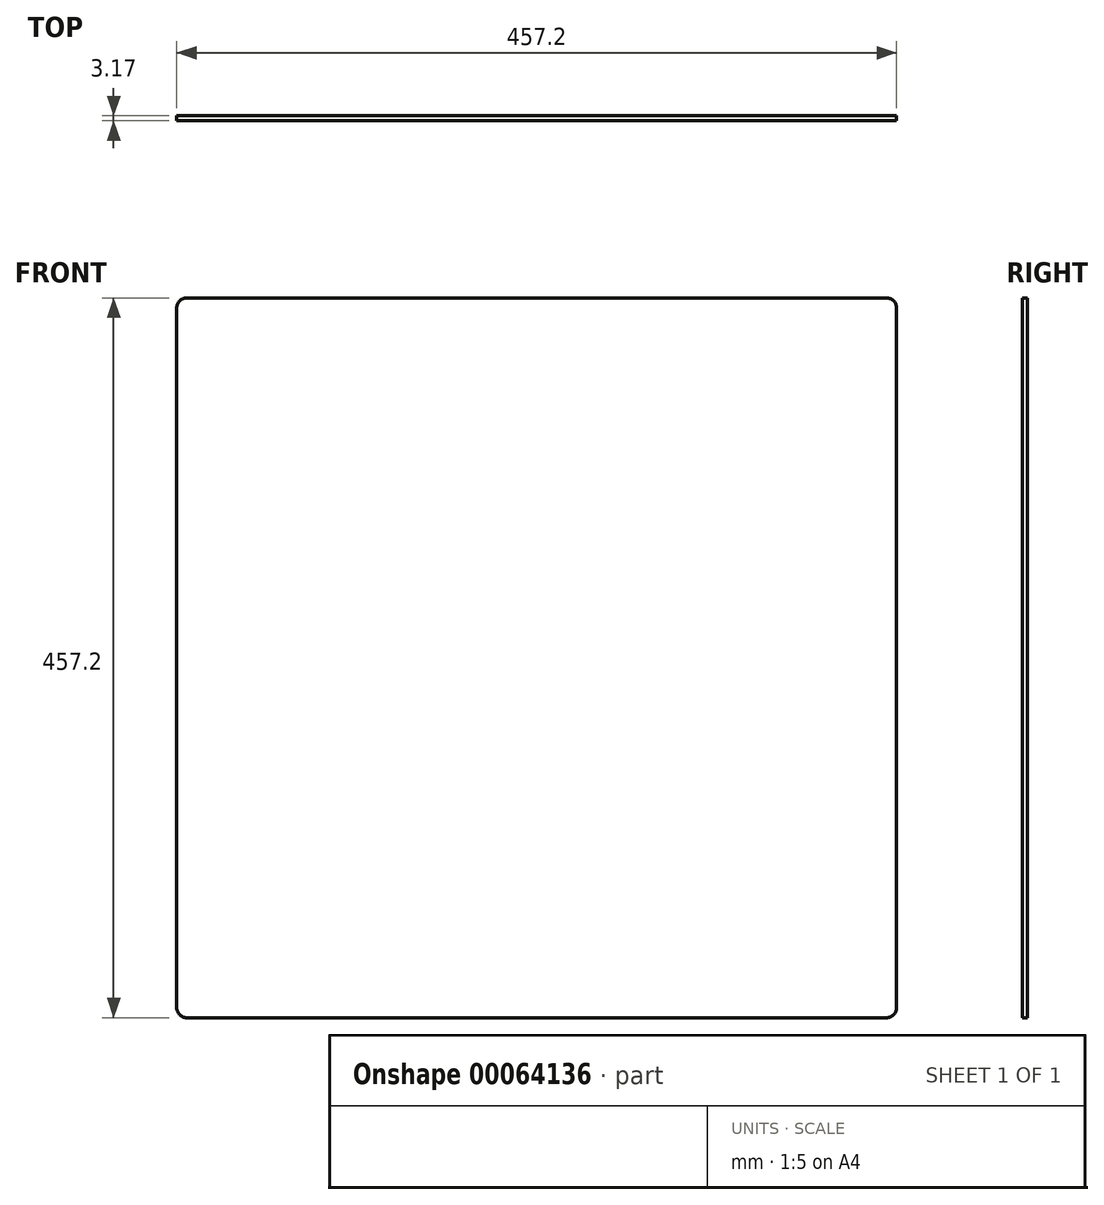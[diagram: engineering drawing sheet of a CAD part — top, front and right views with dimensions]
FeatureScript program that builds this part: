
annotation { "Feature Type Name" : "Feature", "Feature Type Description" : "" }
export const myFeature = defineFeature(function(context is Context, id is Id, definition is map)
    precondition{}
    {
        {
            var Q0;
            Q0=qCreatedBy(makeId("Front.planeOp"),FACE);
            var sketch = newSketch(context, id + "F0", { "sketchPlane" : qUnion([Q0])});
            skLineSegment(sketch, "E0.rect.bottom", {"start": v(-222.25, 228.6) * mm, "end": v(222.25, 228.6) * mm});
            skLineSegment(sketch, "E0.rect.top", {"start": v(-222.25, -228.6) * mm, "end": v(222.25, -228.6) * mm});
            skLineSegment(sketch, "E0.rect.left", {"start": v(-228.6, 222.25) * mm, "end": v(-228.6, -222.25) * mm});
            skLineSegment(sketch, "E0.rect.right", {"start": v(228.6, 222.25) * mm, "end": v(228.6, -222.25) * mm});
            skPoint(sketch, "E0.rect.middle", {"position": v(0, 0) * mm});
            skPoint(sketch, "E1.visualSharp", {"position": v(-228.6, 228.6) * mm});
            skArc(sketch, "E1.filletArc", {"start": v(-222.25, 228.6) * mm, "mid": v(-226.74, 226.74) * mm, "end": v(-228.6, 222.25) * mm});
            skPoint(sketch, "E2.visualSharp", {"position": v(228.6, 228.6) * mm});
            skArc(sketch, "E2.filletArc", {"start": v(228.6, 222.25) * mm, "mid": v(226.74, 226.74) * mm, "end": v(222.25, 228.6) * mm});
            skPoint(sketch, "E3.visualSharp", {"position": v(228.6, -228.6) * mm});
            skArc(sketch, "E3.filletArc", {"start": v(222.25, -228.6) * mm, "mid": v(226.74, -226.74) * mm, "end": v(228.6, -222.25) * mm});
            skPoint(sketch, "E4.visualSharp", {"position": v(-228.6, -228.6) * mm});
            skArc(sketch, "E4.filletArc", {"start": v(-228.6, -222.25) * mm, "mid": v(-226.74, -226.74) * mm, "end": v(-222.25, -228.6) * mm});
            skSolve(sketch);
        }
        {
            var Q0;
            Q0=makeQuery(id+"F0.imprint","IMPRINT",FACE,{"disambiguationData":[TD([[makeQuery(id+"F0.imprint","IMPRINT",EDGE,{"derivedFrom":sQuery(id+"F0.wireOp",EDGE,"E0.rect.bottom")}),-1.0]])]});
            extrude(context, id + "F1", {"entities" : qUnion([Q0]), "depth" : 3.17 * mm});
        }
    });
